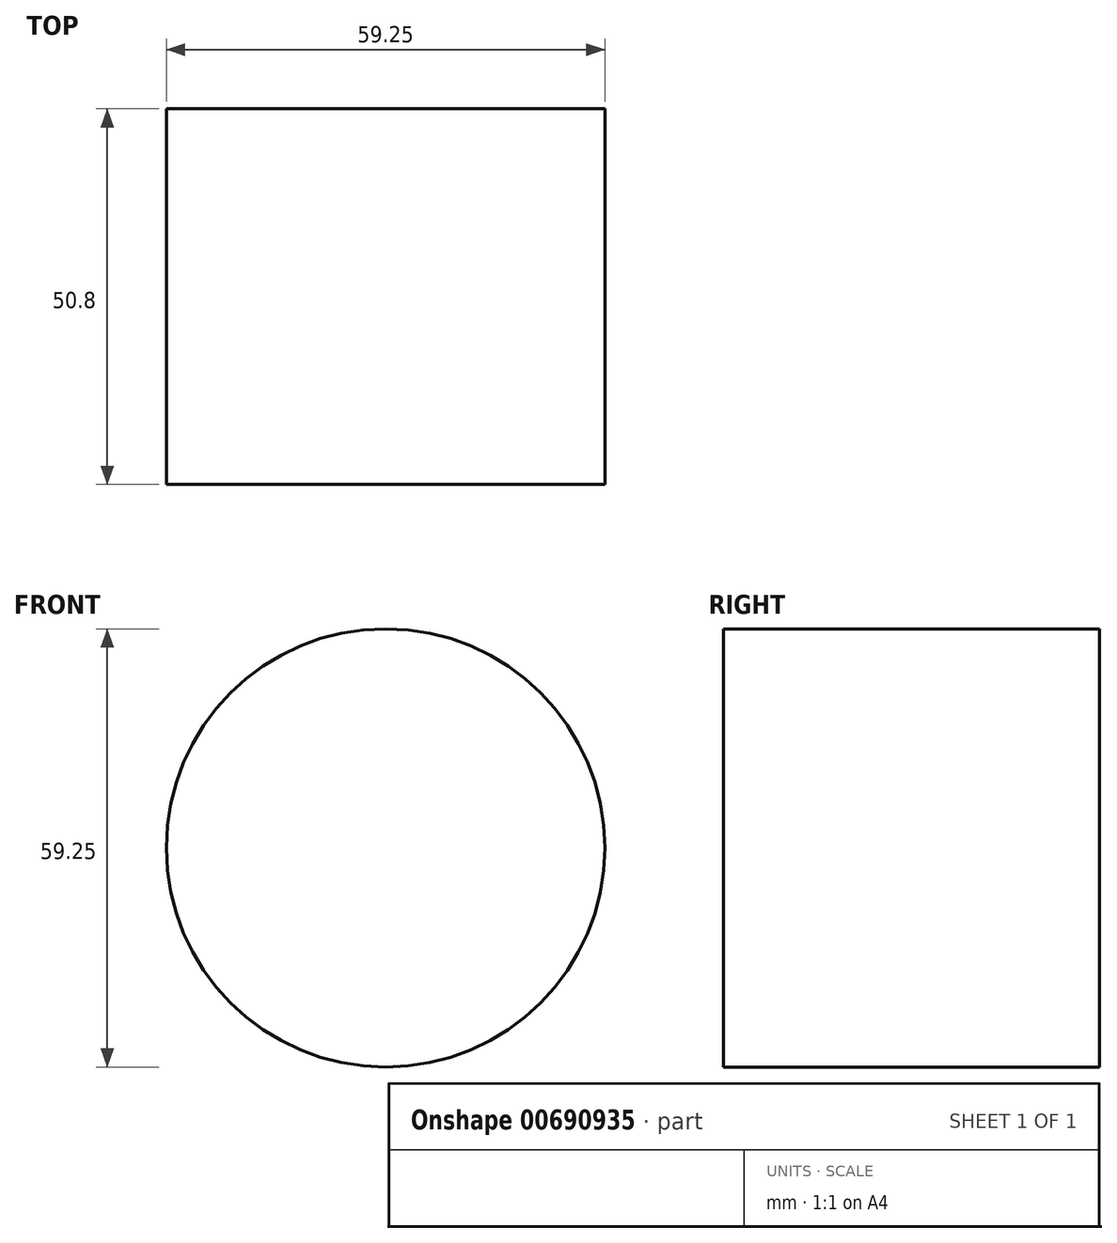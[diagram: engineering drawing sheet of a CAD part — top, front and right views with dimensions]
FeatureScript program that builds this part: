
annotation { "Feature Type Name" : "Feature", "Feature Type Description" : "" }
export const myFeature = defineFeature(function(context is Context, id is Id, definition is map)
    precondition{}
    {
        {
            var Q0;
            Q0=qCreatedBy(makeId("Front.planeOp"),FACE);
            var sketch = newSketch(context, id + "F0", { "sketchPlane" : qUnion([Q0])});
            skCircle(sketch, "E0", {"center": v(0, 0) * mm, "radius": 82.55 * mm});
            skSolve(sketch);
        }
        {
            var Q0;
            Q0=makeQuery(id+"F0.imprint","IMPRINT",FACE,{"disambiguationData":[TD([[makeQuery(id+"F0.imprint","IMPRINT",EDGE,{"derivedFrom":sQuery(id+"F0.wireOp",EDGE,"E0")}),1.0]])]});
            var Q1;
            Q1=sQuery(id+"F0.wireOp",EDGE,"E0");
            extrude(context, id + "F1", {"entities" : qUnion([Q0]), "surfaceEntities" : qUnion([Q1]), "depth" : 50.8 * mm, "offsetDistance" : 25.4 * mm});
        }
        {
            var Q0;
            Q0=makeQuery(id+"F1.opExtrude","CAP_FACE",FACE,{"disambiguationData":[OSD([sQuery(id+"F0.wireOp",EDGE,"E0")])],"isStart":false});
            var sketch = newSketch(context, id + "F2", { "sketchPlane" : qUnion([Q0])});
            skCircle(sketch, "E1", {"center": v(-20.79, 31.37) * mm, "radius": 29.63 * mm});
            skSolve(sketch);
        }
        {
            var Q0;
            Q0=makeQuery(id+"F2.imprint","IMPRINT",FACE,{"disambiguationData":[TD([[makeQuery(id+"F2.imprint","IMPRINT",EDGE,{"derivedFrom":sQuery(id+"F2.wireOp",EDGE,"E1")}),-1.0]])]});
            extrude(context, id + "F3", {"entities" : qUnion([Q0]), "operationType" : NewBodyOperationType.REMOVE, "oppositeDirection" : true, "depth" : 76.2 * mm, "offsetDistance" : 25.4 * mm});
        }
    });
